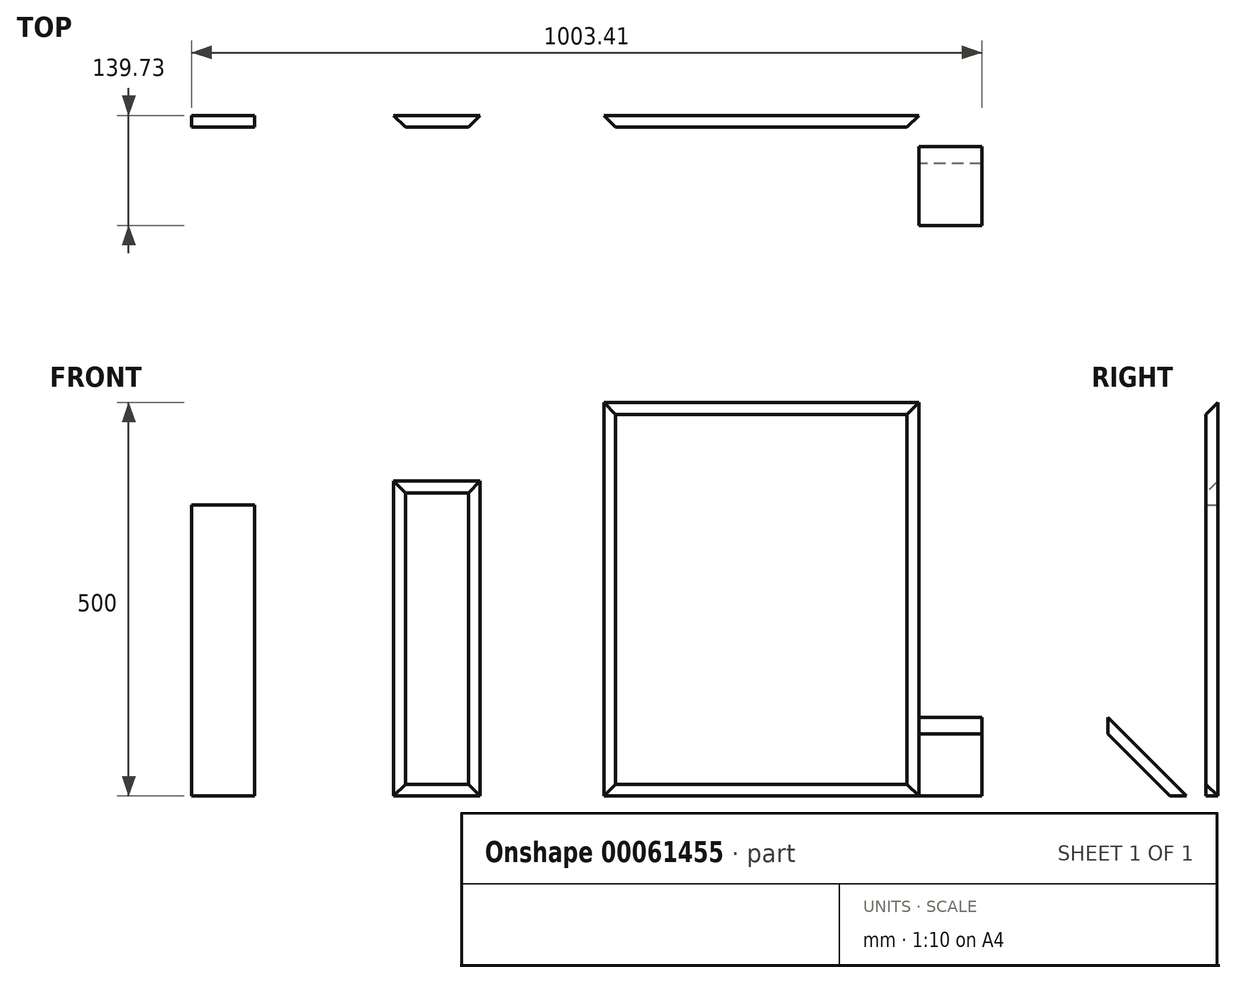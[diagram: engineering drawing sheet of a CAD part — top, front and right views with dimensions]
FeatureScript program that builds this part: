
annotation { "Feature Type Name" : "Feature", "Feature Type Description" : "" }
export const myFeature = defineFeature(function(context is Context, id is Id, definition is map)
    precondition{}
    {
        {
            var Q0;
            Q0=qCreatedBy(makeId("Front.planeOp"),FACE);
            var sketch = newSketch(context, id + "F0", { "sketchPlane" : qUnion([Q0])});
            skLineSegment(sketch, "E0.bottom", {"start": v(0, 0) * mm, "end": v(-400, 0) * mm});
            skLineSegment(sketch, "E0.top", {"start": v(0, 500) * mm, "end": v(-400, 500) * mm});
            skLineSegment(sketch, "E0.left", {"start": v(0, 0) * mm, "end": v(0, 500) * mm});
            skLineSegment(sketch, "E0.right", {"start": v(-400, 0) * mm, "end": v(-400, 500) * mm});
            skSolve(sketch);
        }
        {
            var Q0;
            Q0 = qSketchRegion(id + "F0", true);
            extrude(context, id + "F1", {"entities" : qUnion([Q0]), "depth" : 15 * mm});
        }
        {
            var Q0;
            Q0=qCreatedBy(makeId("Front.planeOp"),FACE);
            var sketch = newSketch(context, id + "F2", { "sketchPlane" : qUnion([Q0])});
            skLineSegment(sketch, "E1.bottom", {"start": v(-557.1, 0) * mm, "end": v(-667.1, 0) * mm});
            skLineSegment(sketch, "E1.top", {"start": v(-557.1, 400) * mm, "end": v(-667.1, 400) * mm});
            skLineSegment(sketch, "E1.left", {"start": v(-557.1, 0) * mm, "end": v(-557.1, 400) * mm});
            skLineSegment(sketch, "E1.right", {"start": v(-667.1, 0) * mm, "end": v(-667.1, 400) * mm});
            skSolve(sketch);
        }
        {
            var Q0;
            Q0 = qSketchRegion(id + "F2", true);
            extrude(context, id + "F3", {"entities" : qUnion([Q0]), "depth" : 15 * mm});
        }
        {
            var Q0;
            Q0=makeQuery(id+"F1.opExtrude","CAP_FACE",FACE,{"disambiguationData":[OSD([sQuery(id+"F0.wireOp",EDGE,"E0.bottom"),sQuery(id+"F0.wireOp",EDGE,"E0.top"),sQuery(id+"F0.wireOp",EDGE,"E0.left"),sQuery(id+"F0.wireOp",EDGE,"E0.right")])],"isStart":false});
            var Q1;
            Q1=makeQuery(id+"F3.opExtrude","CAP_FACE",FACE,{"disambiguationData":[OSD([sQuery(id+"F2.wireOp",EDGE,"E1.bottom"),sQuery(id+"F2.wireOp",EDGE,"E1.top"),sQuery(id+"F2.wireOp",EDGE,"E1.left"),sQuery(id+"F2.wireOp",EDGE,"E1.right")])],"isStart":false});
            chamfer(context, id + "F4", {"entities" : qUnion([Q0, Q1]), "width" : 15 * mm, "tangentPropagation" : true});
        }
        {
            var Q0;
            Q0=qCreatedBy(makeId("Front.planeOp"),FACE);
            var sketch = newSketch(context, id + "F5", { "sketchPlane" : qUnion([Q0])});
            skLineSegment(sketch, "E2.bottom", {"start": v(-843.41, 0) * mm, "end": v(-923.41, 0) * mm});
            skLineSegment(sketch, "E2.top", {"start": v(-843.41, 370) * mm, "end": v(-923.41, 370) * mm});
            skLineSegment(sketch, "E2.left", {"start": v(-843.41, 0) * mm, "end": v(-843.41, 370) * mm});
            skLineSegment(sketch, "E2.right", {"start": v(-923.41, 0) * mm, "end": v(-923.41, 370) * mm});
            skSolve(sketch);
        }
        {
            var Q0;
            Q0 = qSketchRegion(id + "F5", true);
            extrude(context, id + "F6", {"entities" : qUnion([Q0]), "depth" : 15 * mm});
        }
        {
            var Q0;
            Q0=qCreatedBy(makeId("Right.planeOp"),FACE);
            var sketch = newSketch(context, id + "F7", { "sketchPlane" : qUnion([Q0])});
            skLineSegment(sketch, "E3", {"start": v(-39.73, 0) * mm, "end": v(-60.94, 0) * mm});
            skLineSegment(sketch, "E4", {"start": v(-60.94, 0) * mm, "end": v(-139.73, 78.79) * mm});
            skLineSegment(sketch, "E5", {"start": v(-139.73, 100) * mm, "end": v(-39.73, 0) * mm});
            skLineSegment(sketch, "E6", {"start": v(-139.73, 78.79) * mm, "end": v(-139.73, 100) * mm});
            skSolve(sketch);
        }
        {
            var Q0;
            Q0 = qSketchRegion(id + "F7", true);
            extrude(context, id + "F8", {"entities" : qUnion([Q0]), "depth" : 80 * mm});
        }
    });
